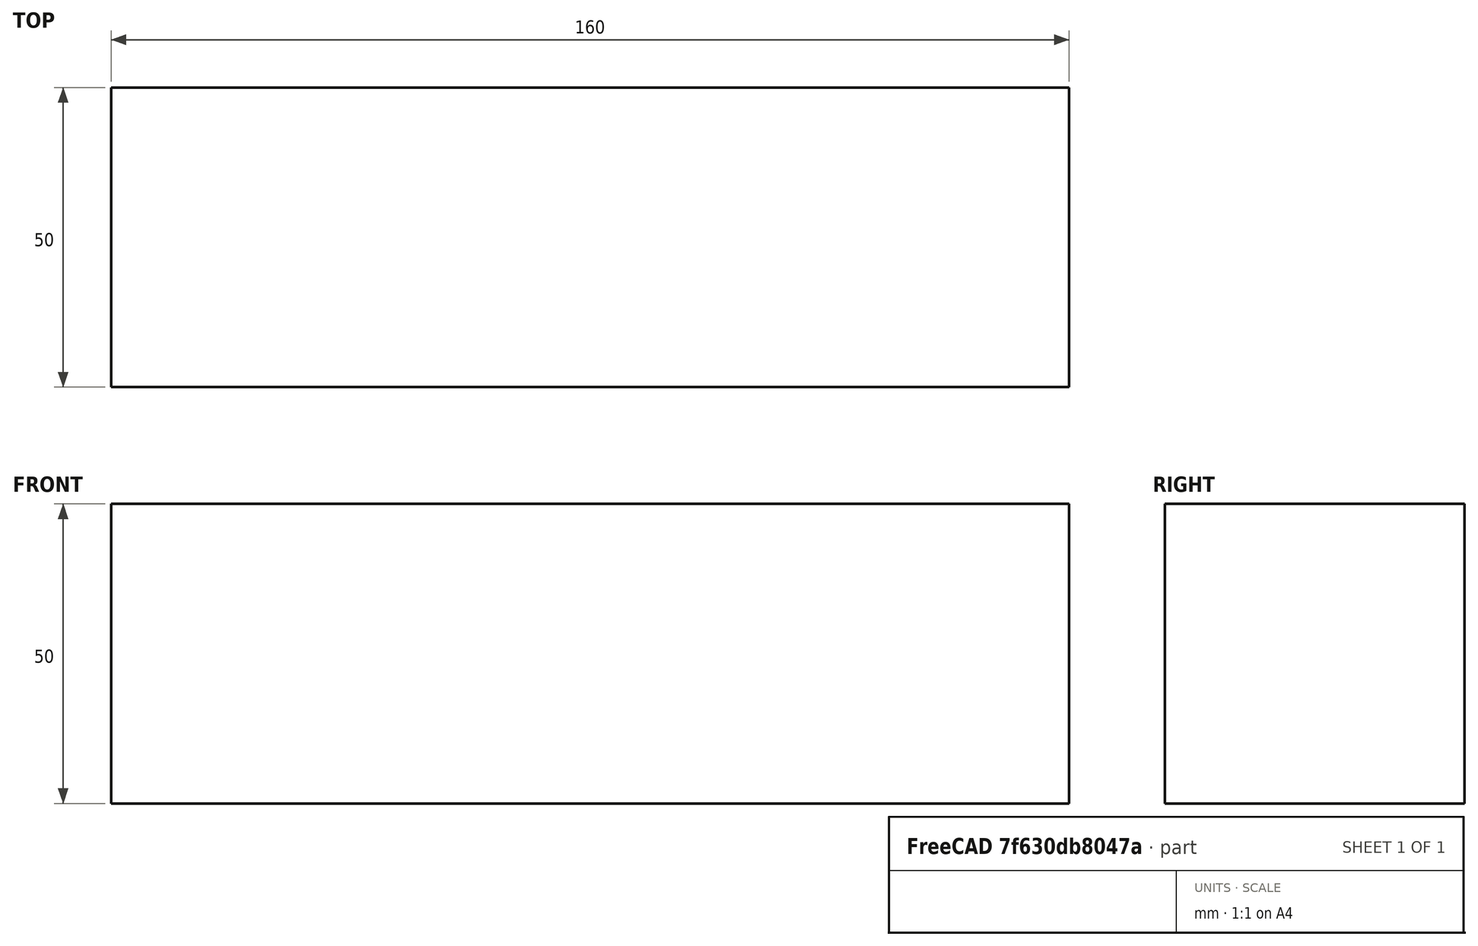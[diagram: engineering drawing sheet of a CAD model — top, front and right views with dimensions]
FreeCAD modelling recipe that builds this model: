
FCSTD DOCUMENT  (FreeCAD 0.15R4671 (Git))
Label: Flat Bar 160x50 EN10058 S235JR
License: All rights reserved
LicenseURL: http://en.wikipedia.org/wiki/All_rights_reserved
objects: Sketcher::SketchObject×1, Part::Extrusion×1
note: 2 computed .brp shape members not serialized (recipe doc carries the construction recipe); baked Part::Feature solids carry a one-line shape summary decoded from their .brp

FEATURE [Sketcher::SketchObject] Sketch
  sketch-geometry (4):
    g0: LineSegment StartX=-80 StartY=-25 StartZ=0 EndX=80 EndY=-25 EndZ=0
    g1: LineSegment StartX=80 StartY=-25 StartZ=0 EndX=80 EndY=25 EndZ=0
    g2: LineSegment StartX=80 StartY=25 StartZ=0 EndX=-80 EndY=25 EndZ=0
    g3: LineSegment StartX=-80 StartY=25 StartZ=0 EndX=-80 EndY=-25 EndZ=0
  constraints (12):
    c: Coincident(g0,g1)
    c: Coincident(g1,g2)
    c: Coincident(g2,g3)
    c: Coincident(g3,g0)
    c: Horizontal(g0)
    c: Horizontal(g2)
    c: Vertical(g1)
    c: Vertical(g3)
    c: Symmetric(g1,g2,g-2)
    c: Symmetric(g0,g1,g-1)
    c: DistanceY(g1) = 50
    c: DistanceX(g0) = 160
FEATURE [Part::Extrusion] Extrude  label="Flat Bar 160x50 EN10058 S235JR"
  Base = -> Sketch
  Dir = (0,0,50)
  Solid = true
